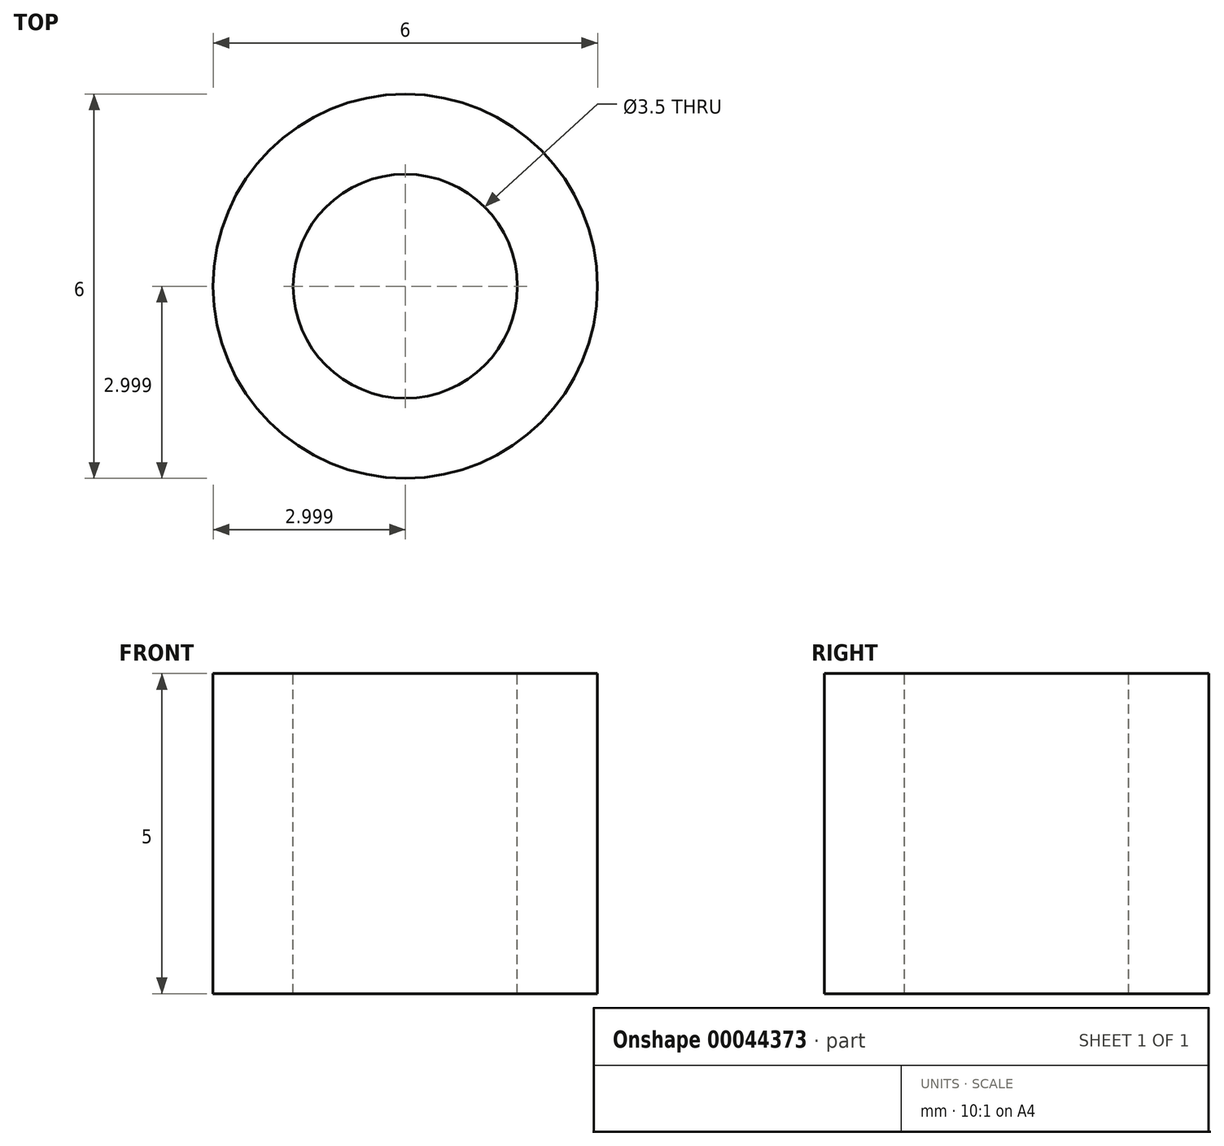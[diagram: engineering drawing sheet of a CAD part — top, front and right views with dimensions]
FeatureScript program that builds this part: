
annotation { "Feature Type Name" : "Feature", "Feature Type Description" : "" }
export const myFeature = defineFeature(function(context is Context, id is Id, definition is map)
    precondition{}
    {
        {
            var Q0;
            Q0=qCreatedBy(makeId("Top.planeOp"),FACE);
            var sketch = newSketch(context, id + "F0", { "sketchPlane" : qUnion([Q0])});
            skCircle(sketch, "E0", {"center": v(-36.21, -53.83) * mm, "radius": 3 * mm});
            skSolve(sketch);
        }
        {
            var Q0;
            Q0=makeQuery(id+"F0.imprint","IMPRINT",FACE,{"disambiguationData":[TD([[makeQuery(id+"F0.imprint","IMPRINT",EDGE,{"derivedFrom":sQuery(id+"F0.wireOp",EDGE,"E0")}),1.0]])]});
            extrude(context, id + "F1", {"entities" : qUnion([Q0]), "depth" : 5 * mm});
        }
        {
            var Q0;
            Q0=makeQuery(id+"F1.opExtrude","CAP_FACE",FACE,{"disambiguationData":[OSD([sQuery(id+"F0.wireOp",EDGE,"E0")])],"isStart":false});
            var sketch = newSketch(context, id + "F2", { "sketchPlane" : qUnion([Q0])});
            skPoint(sketch, "E1", {"position": v(-36.21, -53.83) * mm});
            skSolve(sketch);
        }
        {
            var Q0;
            Q0=sQuery(id+"F2.wireOp",VERTEX,"E1");
            var Q1;
            Q1=makeQuery(id+"F1.opExtrude","SWEPT_BODY",BODY,{"disambiguationData":[OSD([sQuery(id+"F0.wireOp",EDGE,"E0")])]});
            hole(context, id + "F3", {"style" : HoleStyle.SIMPLE, "holeDiameter" : 3.5 * mm, "endStyle" : HoleEndStyle.THROUGH, "locations" : qUnion([Q0]), "scope" : qUnion([Q1])});
        }
    });
